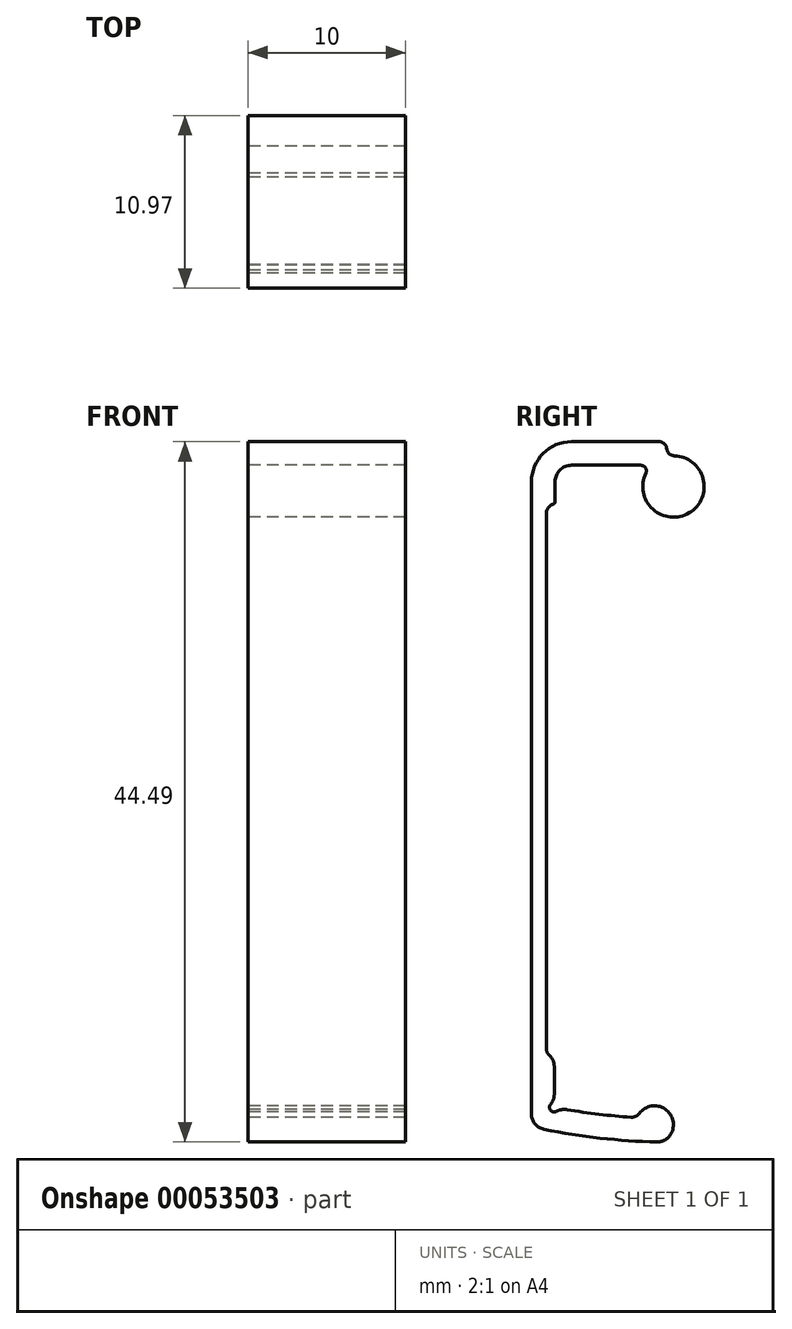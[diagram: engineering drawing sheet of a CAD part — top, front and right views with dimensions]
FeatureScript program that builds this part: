
annotation { "Feature Type Name" : "Feature", "Feature Type Description" : "" }
export const myFeature = defineFeature(function(context is Context, id is Id, definition is map)
    precondition{}
    {
        {
            var Q0;
            Q0=qCreatedBy(makeId("Right.planeOp"),FACE);
            var sketch = newSketch(context, id + "F0", { "sketchPlane" : qUnion([Q0])});
            skLineSegment(sketch, "E0.bottom", {"start": v(9.1, 40) * mm, "end": v(409.1, 40) * mm});
            skLineSegment(sketch, "E0.top", {"start": v(9.1, 21) * mm, "end": v(409.1, 21) * mm});
            skLineSegment(sketch, "E0.left", {"start": v(9.1, 40) * mm, "end": v(9.1, 21) * mm});
            skLineSegment(sketch, "E0.right", {"start": v(409.1, 40) * mm, "end": v(409.1, 21) * mm});
            skSolve(sketch);
        }
        {
            var Q0;
            Q0=qCreatedBy(makeId("Right.planeOp"),FACE);
            var sketch = newSketch(context, id + "F1", { "sketchPlane" : qUnion([Q0])});
            skLineSegment(sketch, "E1.bottom", {"start": v(-0.5, 35) * mm, "end": v(-4.5, 35) * mm});
            skLineSegment(sketch, "E1.top", {"start": v(-0.5, 0) * mm, "end": v(-4.5, 0) * mm});
            skLineSegment(sketch, "E1.left", {"start": v(0, 34.5) * mm, "end": v(0, 0.5) * mm});
            skLineSegment(sketch, "E1.right", {"start": v(-5, 34.5) * mm, "end": v(-5, 0.5) * mm});
            skPoint(sketch, "E2.visualSharp", {"position": v(0, 35) * mm});
            skArc(sketch, "E2.filletArc", {"start": v(0, 34.5) * mm, "mid": v(-0.15, 34.85) * mm, "end": v(-0.5, 35) * mm});
            skPoint(sketch, "E3.visualSharp", {"position": v(-5, 35) * mm});
            skArc(sketch, "E3.filletArc", {"start": v(-4.5, 35) * mm, "mid": v(-4.85, 34.85) * mm, "end": v(-5, 34.5) * mm});
            skPoint(sketch, "E4.visualSharp", {"position": v(-5, 0) * mm});
            skArc(sketch, "E4.filletArc", {"start": v(-5, 0.5) * mm, "mid": v(-4.85, 0.15) * mm, "end": v(-4.5, 0) * mm});
            skPoint(sketch, "E5.visualSharp", {"position": v(0, 0) * mm});
            skArc(sketch, "E5.filletArc", {"start": v(-0.5, 0) * mm, "mid": v(-0.15, 0.15) * mm, "end": v(0, 0.5) * mm});
            skLineSegment(sketch, "E6", {"start": v(-5, 17.5) * mm, "end": v(0, 17.5) * mm, "construction": true});
            skLineSegment(sketch, "E7.rect.bottom", {"start": v(-2.5, 36) * mm, "end": v(-2.5, 36) * mm});
            skLineSegment(sketch, "E7.rect.top", {"start": v(-1.5, 34) * mm, "end": v(-3.5, 34) * mm, "construction": true});
            skLineSegment(sketch, "E7.rect.left", {"start": v(-1.5, 35) * mm, "end": v(-1.5, 34) * mm, "construction": true});
            skLineSegment(sketch, "E7.rect.right", {"start": v(-3.5, 35) * mm, "end": v(-3.5, 34) * mm, "construction": true});
            skPoint(sketch, "E7.rect.middle", {"position": v(-2.5, 35) * mm});
            skPoint(sketch, "E8.visualSharp", {"position": v(-3.5, 36) * mm});
            skArc(sketch, "E8.filletArc", {"start": v(-2.5, 36) * mm, "mid": v(-3.2, 35.7) * mm, "end": v(-3.5, 35) * mm, "construction": true});
            skPoint(sketch, "E9.visualSharp", {"position": v(-1.5, 36) * mm});
            skArc(sketch, "E9.filletArc", {"start": v(-1.5, 35) * mm, "mid": v(-1.8, 35.7) * mm, "end": v(-2.5, 36) * mm, "construction": true});
            skPoint(sketch, "E10.MirrorP", {"position": v(-2.5, 0) * mm});
            skPoint(sketch, "E11.MirrorP", {"position": v(-1.5, -1) * mm});
            skArc(sketch, "E12.MirrorCS", {"start": v(-1.5, 0) * mm, "mid": v(-1.8, -0.7) * mm, "end": v(-2.5, -1) * mm, "construction": true});
            skPoint(sketch, "E13.MirrorP", {"position": v(-3.5, -1) * mm});
            skLineSegment(sketch, "E14.MirrorCS", {"start": v(-2.5, -1) * mm, "end": v(-2.5, -1) * mm});
            skArc(sketch, "E15.MirrorCS", {"start": v(-2.5, -1) * mm, "mid": v(-3.2, -0.7) * mm, "end": v(-3.5, 0) * mm, "construction": true});
            skLineSegment(sketch, "E16.MirrorCS", {"start": v(-3.5, 0) * mm, "end": v(-3.5, 1) * mm, "construction": true});
            skLineSegment(sketch, "E17.MirrorCS", {"start": v(-1.5, 1) * mm, "end": v(-3.5, 1) * mm, "construction": true});
            skLineSegment(sketch, "E18.MirrorCS", {"start": v(-1.5, 0) * mm, "end": v(-1.5, 1) * mm, "construction": true});
            skLineSegment(sketch, "E19.rect.bottom", {"start": v(-4.5, 29.4) * mm, "end": v(-5, 29.4) * mm});
            skLineSegment(sketch, "E19.rect.top", {"start": v(-4.5, 5.6) * mm, "end": v(-5, 5.6) * mm});
            skLineSegment(sketch, "E19.rect.left", {"start": v(-4.5, 29.4) * mm, "end": v(-4.5, 5.6) * mm, "construction": true});
            skPoint(sketch, "E19.rect.middle", {"position": v(-5, 17.5) * mm});
            skPoint(sketch, "E19.rect.right.end.orphan", {"position": v(-5.5, 5.6) * mm});
            skPoint(sketch, "E19.rect.right.start.orphan", {"position": v(-5.5, 29.4) * mm});
            skSolve(sketch);
        }
        {
            var Q0;
            Q0=qCreatedBy(makeId("Right.planeOp"),FACE);
            var sketch = newSketch(context, id + "F2", { "sketchPlane" : qUnion([Q0])});
            skLineSegment(sketch, "E20", {"start": v(-4.2, 35.5) * mm, "end": v(-3.8, 35.5) * mm});
            skLineSegment(sketch, "E21", {"start": v(0, 35.2) * mm, "end": v(0, -0.2) * mm});
            skLineSegment(sketch, "E22", {"start": v(-0.3, -0.5) * mm, "end": v(-1.2, -0.5) * mm});
            skLineSegment(sketch, "E23", {"start": v(-4.5, -0.8) * mm, "end": v(-4.5, -1.5) * mm});
            skLineSegment(sketch, "E24", {"start": v(-3.5, -2.5) * mm, "end": v(3, -2.5) * mm, "construction": true});
            skLineSegment(sketch, "E25", {"start": v(-4.5, 35.8) * mm, "end": v(-4.5, 36.5) * mm});
            skLineSegment(sketch, "E26", {"start": v(-3.5, 37.5) * mm, "end": v(0.9, 37.5) * mm});
            skLineSegment(sketch, "E27", {"start": v(-3.5, 35.8) * mm, "end": v(-3.5, 36.05) * mm});
            skLineSegment(sketch, "E28", {"start": v(-3.5, 36.05) * mm, "end": v(-1.5, 36.05) * mm});
            skLineSegment(sketch, "E29", {"start": v(-1.5, 36.05) * mm, "end": v(-1.5, 35.8) * mm});
            skLineSegment(sketch, "E30.trimOffspring", {"start": v(-1.2, 35.5) * mm, "end": v(-0.3, 35.5) * mm});
            skLineSegment(sketch, "E31.MirrorCS", {"start": v(-1.5, -1.05) * mm, "end": v(-1.5, -0.8) * mm});
            skLineSegment(sketch, "E32.MirrorCS", {"start": v(-3.5, -0.8) * mm, "end": v(-3.5, -1.05) * mm});
            skLineSegment(sketch, "E33.MirrorCS", {"start": v(-3.5, -1.05) * mm, "end": v(-1.5, -1.05) * mm});
            skLineSegment(sketch, "E34.trimOffspring", {"start": v(-3.8, -0.5) * mm, "end": v(-4.2, -0.5) * mm});
            skPoint(sketch, "E35.visualSharp", {"position": v(-4.5, 35.5) * mm});
            skArc(sketch, "E35.filletArc", {"start": v(-4.5, 35.8) * mm, "mid": v(-4.41, 35.59) * mm, "end": v(-4.2, 35.5) * mm});
            skPoint(sketch, "E36.visualSharp", {"position": v(-3.5, 35.5) * mm});
            skArc(sketch, "E36.filletArc", {"start": v(-3.8, 35.5) * mm, "mid": v(-3.59, 35.59) * mm, "end": v(-3.5, 35.8) * mm});
            skPoint(sketch, "E37.visualSharp", {"position": v(0, 35.5) * mm});
            skArc(sketch, "E37.filletArc", {"start": v(0, 35.2) * mm, "mid": v(-0.09, 35.41) * mm, "end": v(-0.3, 35.5) * mm});
            skPoint(sketch, "E38.visualSharp", {"position": v(-1.5, 35.5) * mm});
            skArc(sketch, "E38.filletArc", {"start": v(-1.5, 35.8) * mm, "mid": v(-1.41, 35.59) * mm, "end": v(-1.2, 35.5) * mm});
            skPoint(sketch, "E39.visualSharp", {"position": v(-4.5, -0.5) * mm});
            skArc(sketch, "E39.filletArc", {"start": v(-4.2, -0.5) * mm, "mid": v(-4.41, -0.59) * mm, "end": v(-4.5, -0.8) * mm});
            skPoint(sketch, "E40.visualSharp", {"position": v(-3.5, -0.5) * mm});
            skArc(sketch, "E40.filletArc", {"start": v(-3.5, -0.8) * mm, "mid": v(-3.59, -0.59) * mm, "end": v(-3.8, -0.5) * mm});
            skPoint(sketch, "E41.visualSharp", {"position": v(-1.5, -0.5) * mm});
            skArc(sketch, "E41.filletArc", {"start": v(-1.2, -0.5) * mm, "mid": v(-1.41, -0.59) * mm, "end": v(-1.5, -0.8) * mm});
            skPoint(sketch, "E42.visualSharp", {"position": v(0, -0.5) * mm});
            skArc(sketch, "E42.filletArc", {"start": v(-0.3, -0.5) * mm, "mid": v(-0.09, -0.41) * mm, "end": v(0, -0.2) * mm});
            skArc(sketch, "E43", {"start": v(1.17, 37.07) * mm, "mid": v(2.4, 34.28) * mm, "end": v(4.95, 35.94) * mm});
            skArc(sketch, "E44", {"start": v(3.77, 32.28) * mm, "mid": v(5.44, 33.05) * mm, "end": v(6.58, 34.49) * mm});
            skLineSegment(sketch, "E45", {"start": v(5.5, 36.2) * mm, "end": v(5.25, 36.2) * mm});
            skPoint(sketch, "E46.visualSharp", {"position": v(1.45, 37.5) * mm});
            skArc(sketch, "E46.filletArc", {"start": v(1.17, 37.07) * mm, "mid": v(1.15, 37.36) * mm, "end": v(0.9, 37.5) * mm});
            skPoint(sketch, "E47.visualSharp", {"position": v(4.97, 36.2) * mm});
            skArc(sketch, "E47.filletArc", {"start": v(5.25, 36.2) * mm, "mid": v(5.05, 36.13) * mm, "end": v(4.95, 35.94) * mm});
            skPoint(sketch, "E48.visualSharp", {"position": v(6.97, 36.2) * mm});
            skArc(sketch, "E48.filletArc", {"start": v(6.58, 34.49) * mm, "mid": v(6.51, 35.64) * mm, "end": v(5.5, 36.2) * mm});
            skPoint(sketch, "E49.visualSharp", {"position": v(2.97, 32.2) * mm});
            skArc(sketch, "E49.filletArc", {"start": v(3.77, 32.28) * mm, "mid": v(3.2, 31.93) * mm, "end": v(2.97, 31.3) * mm});
            skPoint(sketch, "E50.visualSharp", {"position": v(-4.5, 37.5) * mm});
            skArc(sketch, "E50.filletArc", {"start": v(-3.5, 37.5) * mm, "mid": v(-4.2, 37.2) * mm, "end": v(-4.5, 36.5) * mm});
            skPoint(sketch, "E51.visualSharp", {"position": v(-4.5, -2.5) * mm});
            skArc(sketch, "E51.filletArc", {"start": v(-4.5, -1.5) * mm, "mid": v(-4.26, -2.15) * mm, "end": v(-3.65, -2.49) * mm});
            skArc(sketch, "E52", {"start": v(4.02, -3.14) * mm, "mid": v(-6.12, -2.09) * mm, "end": v(-15.65, 1.53) * mm, "construction": true});
            skLineSegment(sketch, "E53", {"start": v(-3.65, -2.49) * mm, "end": v(-1.02, -2.88) * mm});
            skArc(sketch, "E54", {"start": v(-0.25, -3.48) * mm, "mid": v(0.3, -3.85) * mm, "end": v(0.86, -3.49) * mm});
            skLineSegment(sketch, "E55", {"start": v(1.5, -2.92) * mm, "end": v(2.25, -2.71) * mm});
            skPoint(sketch, "E56.visualSharp", {"position": v(-0.23, -3) * mm});
            skArc(sketch, "E56.filletArc", {"start": v(-0.25, -3.48) * mm, "mid": v(-0.55, -3.08) * mm, "end": v(-1.02, -2.88) * mm});
            skPoint(sketch, "E57.visualSharp", {"position": v(0.89, -3.1) * mm});
            skArc(sketch, "E57.filletArc", {"start": v(1.5, -2.92) * mm, "mid": v(1.12, -3.13) * mm, "end": v(0.86, -3.49) * mm});
            skPoint(sketch, "E58.visualSharp", {"position": v(3, -2.5) * mm});
            skArc(sketch, "E58.filletArc", {"start": v(2.18, -2.73) * mm, "mid": v(2.93, -1.9) * mm, "end": v(2.45, -0.9) * mm});
            skLineSegment(sketch, "E59", {"start": v(2, -0.64) * mm, "end": v(6.12, 6.46) * mm});
            skLineSegment(sketch, "E60", {"start": v(6.7, 35) * mm, "end": v(6.7, -7.44) * mm, "construction": true});
            skLineSegment(sketch, "E61", {"start": v(2.45, -0.9) * mm, "end": v(2, -0.64) * mm});
            skLineSegment(sketch, "E62", {"start": v(6.12, 6.46) * mm, "end": v(6.55, 6.2) * mm});
            skLineSegment(sketch, "E63", {"start": v(6.7, 6.3) * mm, "end": v(6.7, 8.3) * mm});
            skLineSegment(sketch, "E64", {"start": v(5.7, 9.3) * mm, "end": v(3.47, 9.3) * mm});
            skPoint(sketch, "E65.visualSharp", {"position": v(6.7, 9.3) * mm});
            skArc(sketch, "E65.filletArc", {"start": v(6.7, 8.3) * mm, "mid": v(6.4, 9) * mm, "end": v(5.7, 9.3) * mm});
            skLineSegment(sketch, "E66.trimOffspring", {"start": v(2.97, 9.8) * mm, "end": v(2.97, 31.3) * mm});
            skPoint(sketch, "E67.visualSharp", {"position": v(6.7, 6.12) * mm});
            skArc(sketch, "E67.filletArc", {"start": v(6.55, 6.2) * mm, "mid": v(6.65, 6.2) * mm, "end": v(6.7, 6.3) * mm});
            skPoint(sketch, "E68.visualSharp", {"position": v(2.97, 9.3) * mm});
            skArc(sketch, "E68.filletArc", {"start": v(2.97, 9.8) * mm, "mid": v(3.11, 9.45) * mm, "end": v(3.47, 9.3) * mm});
            skSolve(sketch);
        }
        {
            var Q0;
            Q0=qCreatedBy(makeId("Right.planeOp"),FACE);
            var sketch = newSketch(context, id + "F3", { "sketchPlane" : qUnion([Q0])});
            skArc(sketch, "E69.0", {"start": v(1.21, 37.05) * mm, "mid": v(3.98, 34.53) * mm, "end": v(3.03, 38.15) * mm});
            skLineSegment(sketch, "E69.1", {"start": v(-4.55, 35.22) * mm, "end": v(-4.55, 36.5) * mm});
            skArc(sketch, "E69.2", {"start": v(-3.5, 37.55) * mm, "mid": v(-4.24, 37.24) * mm, "end": v(-4.55, 36.5) * mm});
            skLineSegment(sketch, "E69.3", {"start": v(-3.5, 37.55) * mm, "end": v(0.9, 37.55) * mm});
            skArc(sketch, "E69.4", {"start": v(1.21, 37.05) * mm, "mid": v(1.2, 37.39) * mm, "end": v(0.9, 37.55) * mm});
            skLineSegment(sketch, "E70.0", {"start": v(-5.1, 34.5) * mm, "end": v(-5.1, 0.5) * mm});
            skArc(sketch, "E70.1", {"start": v(-4.66, 35.08) * mm, "mid": v(-4.98, 34.86) * mm, "end": v(-5.1, 34.5) * mm});
            skLineSegment(sketch, "E71.0", {"start": v(-3.5, 39.05) * mm, "end": v(2.05, 39.05) * mm});
            skArc(sketch, "E71.1", {"start": v(-3.5, 39.05) * mm, "mid": v(-5.3, 38.3) * mm, "end": v(-6.05, 36.5) * mm});
            skLineSegment(sketch, "E72", {"start": v(2.55, 38.56) * mm, "end": v(2.54, 38.64) * mm});
            skLineSegment(sketch, "E73", {"start": v(2.97, 36.2) * mm, "end": v(2.97, 41) * mm, "construction": true});
            skLineSegment(sketch, "E74", {"start": v(-6.05, 36.5) * mm, "end": v(-6.05, -3.65) * mm});
            skPoint(sketch, "E75.visualSharp", {"position": v(2.47, 39.05) * mm});
            skArc(sketch, "E75.filletArc", {"start": v(2.54, 38.64) * mm, "mid": v(2.37, 38.93) * mm, "end": v(2.05, 39.05) * mm});
            skPoint(sketch, "E76.visualSharp", {"position": v(2.63, 38.12) * mm});
            skArc(sketch, "E76.filletArc", {"start": v(2.55, 38.56) * mm, "mid": v(2.72, 38.27) * mm, "end": v(3.03, 38.15) * mm});
            skPoint(sketch, "E77.visualSharp", {"position": v(-4.55, 35.1) * mm});
            skArc(sketch, "E77.filletArc", {"start": v(-4.66, 35.08) * mm, "mid": v(-4.58, 35.13) * mm, "end": v(-4.55, 35.22) * mm});
            skArc(sketch, "E78", {"start": v(-3.8, -3.38) * mm, "mid": v(-1.76, -3.67) * mm, "end": v(0.28, -3.86) * mm});
            skArc(sketch, "E79", {"start": v(2.8, -4.96) * mm, "mid": v(2.44, -3.34) * mm, "end": v(0.8, -3.62) * mm});
            skArc(sketch, "E80.0", {"start": v(-5.25, -4.63) * mm, "mid": v(-1.68, -5.2) * mm, "end": v(1.91, -5.44) * mm});
            skPoint(sketch, "E81.trimOffspring.end.orphan", {"position": v(-5.05, -5.35) * mm});
            skPoint(sketch, "E82.orphan", {"position": v(-6.05, -5.35) * mm});
            skPoint(sketch, "E83.visualSharp", {"position": v(-6.05, -4.46) * mm});
            skArc(sketch, "E83.filletArc", {"start": v(-6.05, -3.65) * mm, "mid": v(-5.82, -4.29) * mm, "end": v(-5.25, -4.63) * mm});
            skPoint(sketch, "E84.visualSharp", {"position": v(-5.1, -3.13) * mm});
            skArc(sketch, "E85.0", {"start": v(-5.1, 0.5) * mm, "mid": v(-5.05, 0.26) * mm, "end": v(-4.91, 0.06) * mm});
            skLineSegment(sketch, "E86.0", {"start": v(-4.6, -0.66) * mm, "end": v(-4.6, -2.4) * mm});
            skArc(sketch, "E87", {"start": v(-4.83, -3.04) * mm, "mid": v(-4.83, -3.42) * mm, "end": v(-4.45, -3.5) * mm});
            skPoint(sketch, "E88.visualSharp", {"position": v(-4.6, -2.93) * mm});
            skArc(sketch, "E88.filletArc", {"start": v(-4.83, -3.04) * mm, "mid": v(-4.66, -2.74) * mm, "end": v(-4.6, -2.4) * mm});
            skPoint(sketch, "E89.visualSharp", {"position": v(-4.3, -3.29) * mm});
            skArc(sketch, "E89.filletArc", {"start": v(-3.8, -3.38) * mm, "mid": v(-4.13, -3.38) * mm, "end": v(-4.45, -3.5) * mm});
            skPoint(sketch, "E90.visualSharp", {"position": v(-4.6, -0.1) * mm});
            skArc(sketch, "E90.filletArc", {"start": v(-4.6, -0.66) * mm, "mid": v(-4.68, -0.27) * mm, "end": v(-4.91, 0.06) * mm});
            skPoint(sketch, "E91.visualSharp", {"position": v(2.22, -5.44) * mm});
            skArc(sketch, "E91.filletArc", {"start": v(1.91, -5.44) * mm, "mid": v(2.42, -5.32) * mm, "end": v(2.8, -4.96) * mm});
            skPoint(sketch, "E92.visualSharp", {"position": v(0.66, -3.88) * mm});
            skArc(sketch, "E92.filletArc", {"start": v(0.28, -3.86) * mm, "mid": v(0.57, -3.8) * mm, "end": v(0.8, -3.62) * mm});
            skSolve(sketch);
        }
        {
            var Q0;
            Q0 = qSketchRegion(id + "F3", true);
            extrude(context, id + "F4", {"entities" : qUnion([Q0]), "depth" : 10 * mm});
        }
    });
